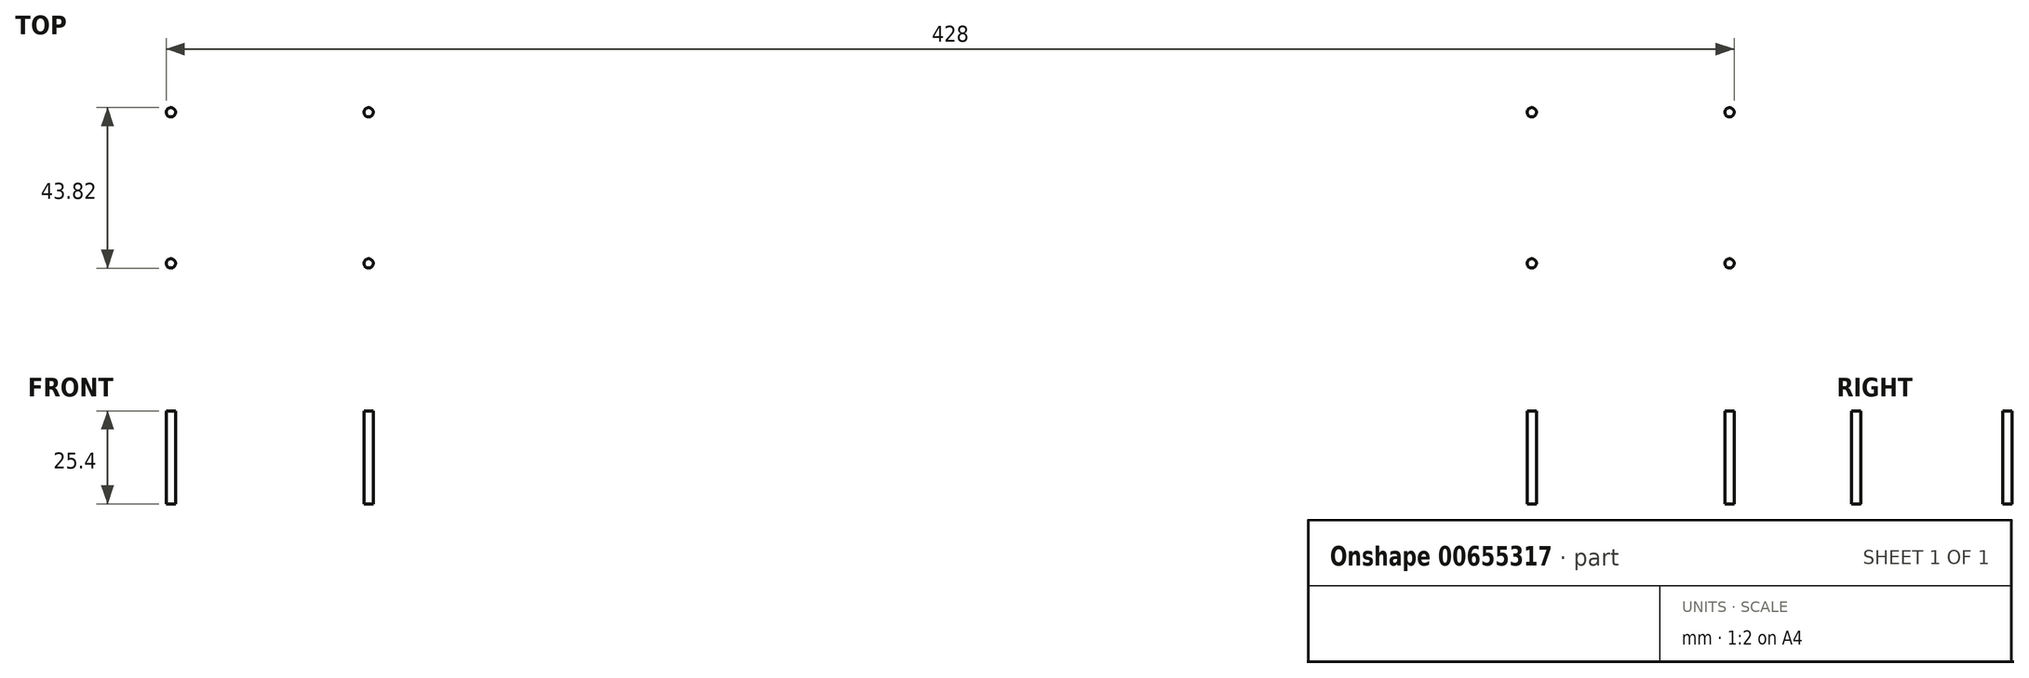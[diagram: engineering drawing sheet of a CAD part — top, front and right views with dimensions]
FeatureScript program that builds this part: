
annotation { "Feature Type Name" : "Feature", "Feature Type Description" : "" }
export const myFeature = defineFeature(function(context is Context, id is Id, definition is map)
    precondition{}
    {
        {
            var Q0;
            Q0=qCreatedBy(makeId("Top.planeOp"),FACE);
            var sketch = newSketch(context, id + "F0", { "sketchPlane" : qUnion([Q0])});
            skCircle(sketch, "E0", {"center": v(158.75, 20.64) * mm, "radius": 1.27 * mm});
            skCircle(sketch, "E1", {"center": v(-158.75, -20.64) * mm, "radius": 1.27 * mm});
            skCircle(sketch, "E2", {"center": v(212.72, -20.64) * mm, "radius": 1.27 * mm});
            skCircle(sketch, "E3", {"center": v(212.72, 20.64) * mm, "radius": 1.27 * mm});
            skCircle(sketch, "E4", {"center": v(-158.75, 20.64) * mm, "radius": 1.27 * mm});
            skCircle(sketch, "E5", {"center": v(158.75, -20.64) * mm, "radius": 1.27 * mm});
            skCircle(sketch, "E6", {"center": v(-212.72, -20.64) * mm, "radius": 1.27 * mm});
            skCircle(sketch, "E7", {"center": v(-212.72, 20.64) * mm, "radius": 1.27 * mm});
            skSolve(sketch);
        }
        {
            var Q0;
            Q0 = qSketchRegion(id + "F0", true);
            extrude(context, id + "F1", {"entities" : qUnion([Q0]), "depth" : 25.4 * mm, "offsetDistance" : 25.4 * mm});
        }
    });
